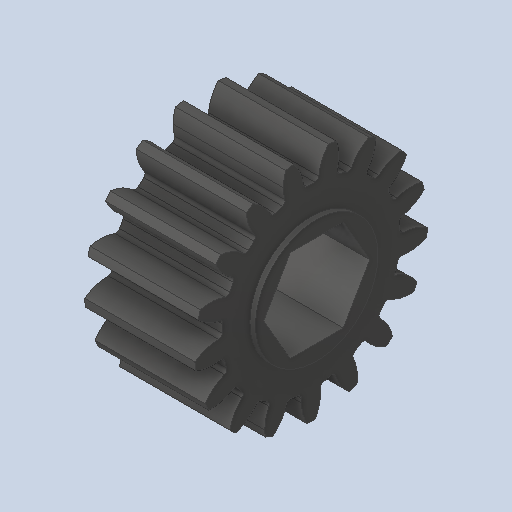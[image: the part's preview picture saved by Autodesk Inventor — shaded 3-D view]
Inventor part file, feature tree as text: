
AUTODESK INVENTOR PART (.ipt)
format: ipt  version: 2023 (Build 270158000, 158)  size: 274,432 bytes
history: native  units: in
note: dims shown in document units (in); Inventor stores cm internally (conversion verified against a paired STEP export)
features: fillet x1
ambient origin geometry x8: Origin, YZ Plane, XZ Plane, XY Plane, X Axis, Y Axis, Z Axis, Center Point
bodies: Solid1 (feature_tree)
feature tree (1):
  fillet  "Fillet1"  [1 undecoded]
note: 1 required parameter value undecoded (feature->parameter linkage not recoverable at this tier; creation-order binding heuristic only, values carry confidence <= 0.55)
